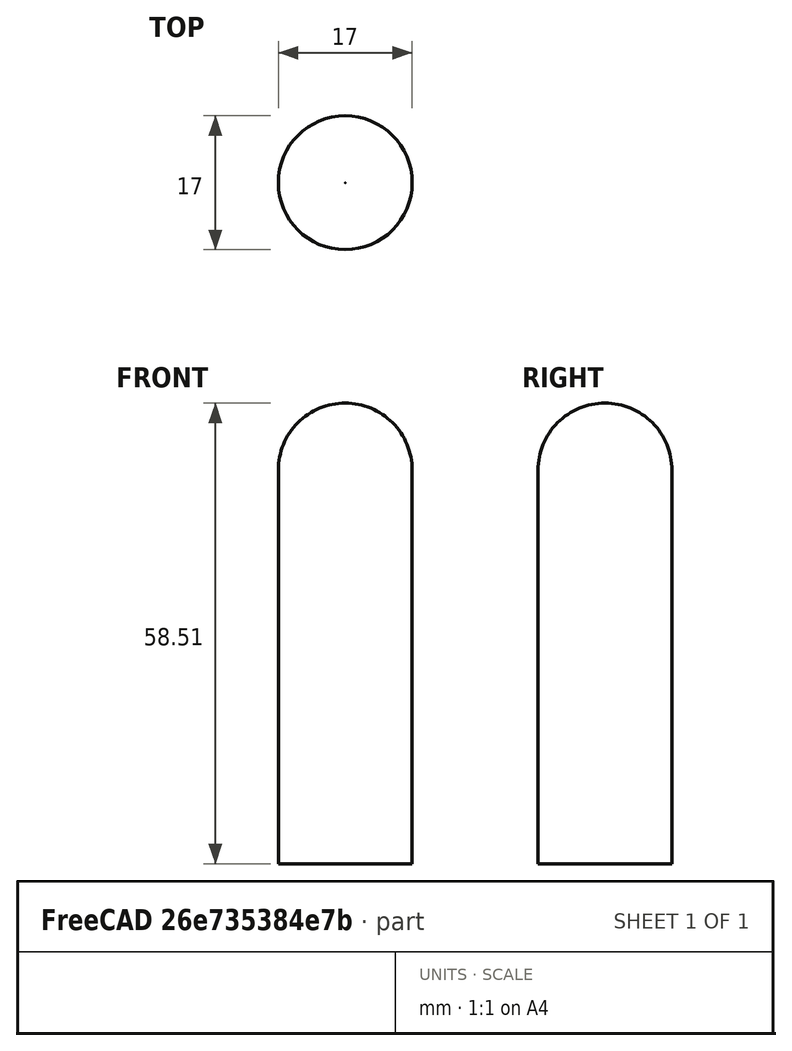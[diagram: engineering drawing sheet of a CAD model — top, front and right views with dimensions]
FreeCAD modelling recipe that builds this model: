
FCSTD DOCUMENT  (FreeCAD 0.20R29177 (Git))
Label: IntestineV1_inner_collisionv1
License: All rights reserved
LicenseURL: http://en.wikipedia.org/wiki/All_rights_reserved
objects: Sketcher::SketchObject×1, Part::Revolution×1, Part::Reverse×1
note: 3 computed .brp shape members not serialized (recipe doc carries the construction recipe); baked Part::Feature solids carry a one-line shape summary decoded from their .brp

FEATURE [Sketcher::SketchObject] Sketch
  FullyConstrained = false
  Placement = pos=(0,0,0) rot=(1,0,0;1.5708rad)
  sketch-geometry (4):
    g0: LineSegment StartX=8.5 StartY=50 StartZ=0 EndX=8.5 EndY=0 EndZ=0
    g1: GeomPoint X=8.5 Y=0 Z=0
    g2: ArcOfCircle CenterX=0 CenterY=50.0107 CenterZ=0 NormalX=0 NormalY=0 NormalZ=1 AngleXU=0 Radius=8.50001 StartAngle=6.28193 EndAngle=7.85382
    g3: LineSegment StartX=8.5 StartY=0 StartZ=0 EndX=0 EndY=0 EndZ=0
  constraints (7):
    c: Parallel(g0,g-2)
    c: Coincident(g1,g0)
    c: PointOnObject(g2,g-2)
    c: Coincident(g2,g0)
    c: Coincident(g3,g0)
    c: Coincident(g3,g-1)
    c: Horizontal(g3)
FEATURE [Part::Revolution] Revolve
  Angle = 360
  Axis = (0,0,1)
  Base = (0,0,0)
  FaceMakerClass = Part::FaceMakerBullseye
  Solid = false
  Source = -> Sketch
  Symmetric = false
FEATURE [Part::Reverse] Revolve_rev  label="Revolve (Rev)"
  Source = -> Revolve
